# Revit family: Table-Teknion-HTMC-upStage_Round_Table-R2022
name_source: partatom
category: Furniture
units: mm (PartAtom-declared; Revit-internal decimal feet)

## family parameters
Always vertical = Yes
Cut with Voids When Loaded = No
OmniClass Number = 23.40.20.00
OmniClass Title = General Furniture and Specialties
Render Appearance Source = Family Geometry
Room Calculation Point = No
Shared = Yes
Work Plane-Based = No

## types (3) — shared parameters
Assembly Code = E2020200
Manufacturer = Teknion
Manufacturer Fax = 416.661.4586
Model = HTMC
Product Documentation Link = https://www.teknion.com
Product Line = Meeting Tables
Product Page URL = https://www.teknion.com
Series = upStage
Sustainability Data = https://www.teknion.com
URL = www.teknion.com
Unit Weight URL = http://www.teknion.com
Warranty = http://www.teknion.com
zero-valued in all types: Default Elevation

## per-type parameters (varying)
| type | 1 | 2 | 48 | 54 | 60 | Description | Part Number | Radius | Width |
| 48" Diameter | 7.303 " | 7.303 " | Yes | No | No | Upstage Round Table, 48" Diameter | HTMC_48_ | 24 " | 48 " |
| 54" Diameter | 8.182 " | 8.182 " | No | Yes | No | Upstage Round Table, 54" Diameter | HTMC_54_ | 27 " | 54 " |
| 60" Diameter | 9.061 " | 9.061 " | No | No | Yes | Upstage Round Table, 60" Diameter | HTMC_60_ | 30 " | 60 " |

## geometry (parser evidence)
native form markers: Sweep x9
no freeform markers — native parametric forms only
